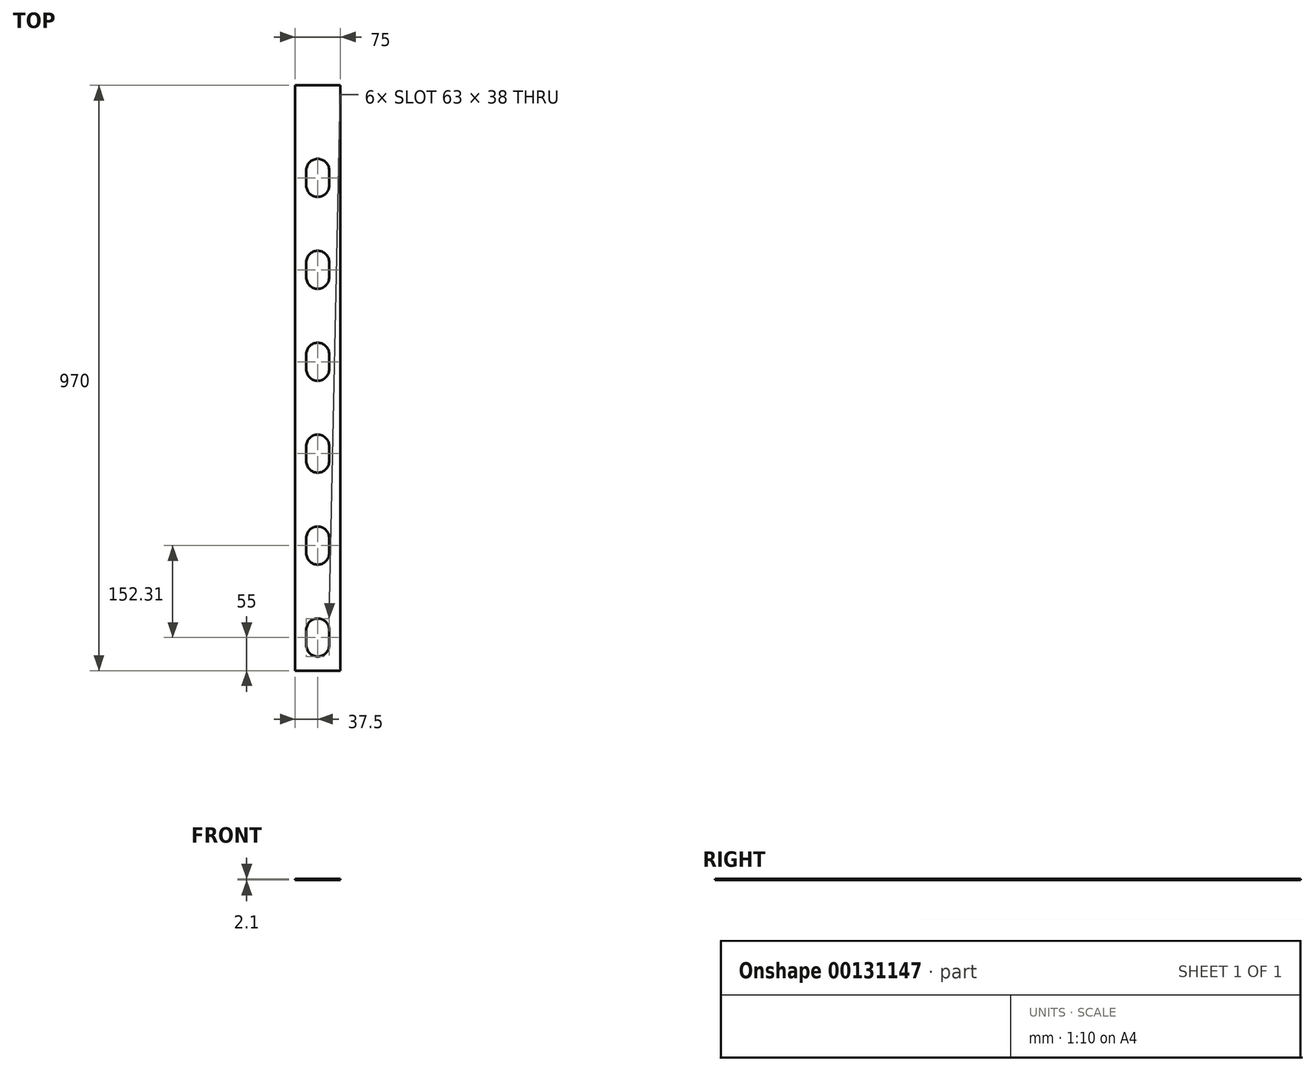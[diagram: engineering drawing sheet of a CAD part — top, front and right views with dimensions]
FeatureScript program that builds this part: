
annotation { "Feature Type Name" : "Feature", "Feature Type Description" : "" }
export const myFeature = defineFeature(function(context is Context, id is Id, definition is map)
    precondition{}
    {
        {
            var Q0;
            Q0=qCreatedBy(makeId("Top.planeOp"),FACE);
            var sketch = newSketch(context, id + "F0", { "sketchPlane" : qUnion([Q0])});
            skLineSegment(sketch, "E0.bottom", {"start": v(37.5, -485) * mm, "end": v(-37.5, -485) * mm});
            skLineSegment(sketch, "E0.top", {"start": v(37.5, 485) * mm, "end": v(-37.5, 485) * mm});
            skLineSegment(sketch, "E0.left", {"start": v(37.5, -485) * mm, "end": v(37.5, 485) * mm});
            skLineSegment(sketch, "E0.right", {"start": v(-37.5, -485) * mm, "end": v(-37.5, 485) * mm});
            skPoint(sketch, "E0.middle", {"position": v(0, 0) * mm});
            skPoint(sketch, "E1.center.orphan", {"position": v(22.25, -0.97) * mm});
            skArc(sketch, "E2", {"start": v(-19, -442.5) * mm, "mid": v(0, -461.5) * mm, "end": v(19, -442.5) * mm});
            skArc(sketch, "E3", {"start": v(19, -417.5) * mm, "mid": v(0, -398.5) * mm, "end": v(-19, -417.5) * mm});
            skLineSegment(sketch, "E4", {"start": v(-19, -417.5) * mm, "end": v(-19, -442.5) * mm});
            skLineSegment(sketch, "E5", {"start": v(19, -417.5) * mm, "end": v(19, -442.5) * mm});
            skArc(sketch, "E6", {"start": v(-19, -290.19) * mm, "mid": v(0, -309.19) * mm, "end": v(19, -290.19) * mm});
            skArc(sketch, "E7", {"start": v(19, -265.2) * mm, "mid": v(0, -246.2) * mm, "end": v(-19, -265.2) * mm});
            skLineSegment(sketch, "E8", {"start": v(-19, -265.2) * mm, "end": v(-19, -290.19) * mm});
            skLineSegment(sketch, "E9", {"start": v(19, -265.2) * mm, "end": v(19, -290.19) * mm});
            skArc(sketch, "E10", {"start": v(-19, -137.88) * mm, "mid": v(0, -156.88) * mm, "end": v(19, -137.88) * mm});
            skArc(sketch, "E11", {"start": v(19, -112.88) * mm, "mid": v(0, -93.88) * mm, "end": v(-19, -112.88) * mm});
            skLineSegment(sketch, "E12", {"start": v(-19, -112.88) * mm, "end": v(-19, -137.88) * mm});
            skLineSegment(sketch, "E13", {"start": v(19, -112.88) * mm, "end": v(19, -137.88) * mm});
            skArc(sketch, "E14", {"start": v(-19, 14.43) * mm, "mid": v(0, -4.57) * mm, "end": v(19, 14.43) * mm});
            skArc(sketch, "E15", {"start": v(19, 39.43) * mm, "mid": v(0, 58.43) * mm, "end": v(-19, 39.43) * mm});
            skLineSegment(sketch, "E16", {"start": v(-19, 39.43) * mm, "end": v(-19, 14.43) * mm});
            skLineSegment(sketch, "E17", {"start": v(19, 39.43) * mm, "end": v(19, 14.43) * mm});
            skArc(sketch, "E18", {"start": v(-19, 166.74) * mm, "mid": v(0, 147.74) * mm, "end": v(19, 166.74) * mm});
            skArc(sketch, "E19", {"start": v(19, 191.74) * mm, "mid": v(0, 210.74) * mm, "end": v(-19, 191.74) * mm});
            skLineSegment(sketch, "E20", {"start": v(-19, 191.74) * mm, "end": v(-19, 166.74) * mm});
            skLineSegment(sketch, "E21", {"start": v(19, 191.74) * mm, "end": v(19, 166.74) * mm});
            skArc(sketch, "E22", {"start": v(-19, 319.05) * mm, "mid": v(0, 300.05) * mm, "end": v(19, 319.05) * mm});
            skArc(sketch, "E23", {"start": v(19, 344.05) * mm, "mid": v(0, 363.05) * mm, "end": v(-19, 344.05) * mm});
            skLineSegment(sketch, "E24", {"start": v(-19, 344.05) * mm, "end": v(-19, 319.05) * mm});
            skLineSegment(sketch, "E25", {"start": v(19, 344.05) * mm, "end": v(19, 319.05) * mm});
            skSolve(sketch);
        }
        {
            var Q0;
            Q0 = qSketchRegion(id + "F0", true);
            var Q1;
            Q1=makeQuery(id+"F0.imprint","IMPRINT",FACE,{"disambiguationData":[TD([[makeQuery(id+"F0.imprint","IMPRINT",EDGE,{"derivedFrom":sQuery(id+"F0.wireOp",EDGE,"E0.bottom")}),-1.0]])]});
            extrude(context, id + "F1", {"entities" : qUnion([Q0, Q1]), "depth" : 2.1 * mm});
        }
    });
